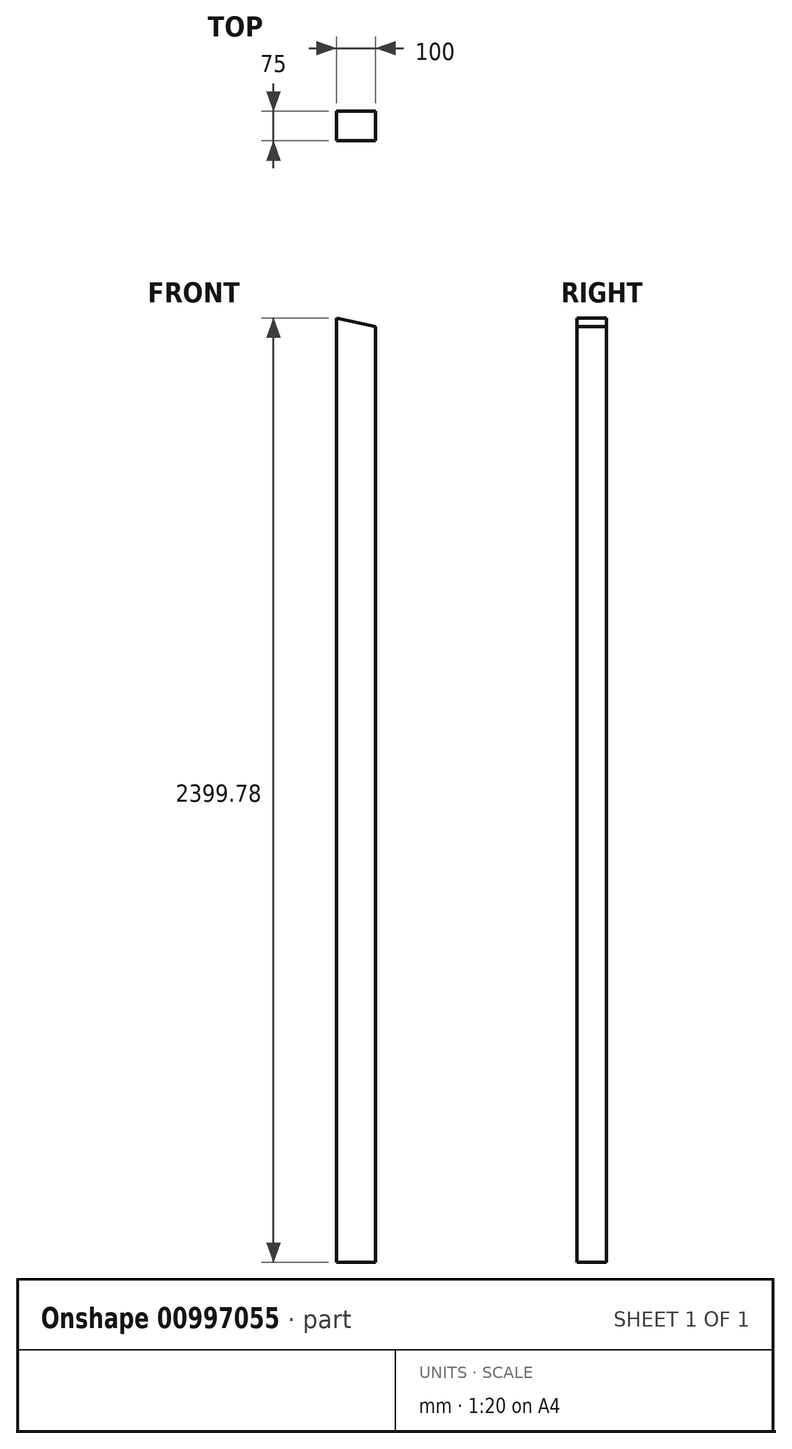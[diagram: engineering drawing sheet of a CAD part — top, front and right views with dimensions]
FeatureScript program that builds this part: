
annotation { "Feature Type Name" : "Feature", "Feature Type Description" : "" }
export const myFeature = defineFeature(function(context is Context, id is Id, definition is map)
    precondition{}
    {
        {
            var Q0;
            Q0=qCreatedBy(makeId("Top.planeOp"),FACE);
            var sketch = newSketch(context, id + "F0", { "sketchPlane" : qUnion([Q0])});
            skLineSegment(sketch, "E0.bottom", {"start": v(-100, 15.8) * mm, "end": v(0, 15.8) * mm});
            skLineSegment(sketch, "E0.top", {"start": v(-100, -59.2) * mm, "end": v(0, -59.2) * mm});
            skLineSegment(sketch, "E0.left", {"start": v(-100, 15.8) * mm, "end": v(-100, -59.2) * mm});
            skLineSegment(sketch, "E0.right", {"start": v(0, 15.8) * mm, "end": v(0, -59.2) * mm});
            skSolve(sketch);
        }
        {
            var Q0;
            Q0=makeQuery(id+"F0.imprint","IMPRINT",FACE,{"disambiguationData":[TD([[makeQuery(id+"F0.imprint","IMPRINT",EDGE,{"derivedFrom":sQuery(id+"F0.wireOp",EDGE,"E0.bottom")}),-1.0]])]});
            extrude(context, id + "F1", {"entities" : qUnion([Q0]), "oppositeDirection" : true, "depth" : 2400 * mm, "offsetDistance" : 25 * mm});
        }
        {
            var Q0;
            Q0=makeQuery(id+"F1.opExtrude","CAP_EDGE",EDGE,{"disambiguationData":[OSD([sQuery(id+"F0.wireOp",EDGE,"E0.right")])],"isStart":true});
            chamfer(context, id + "F2", {"entities" : qUnion([Q0]), "chamferType" : ChamferType.OFFSET_ANGLE, "width" : 101 * mm, "oppositeDirection" : true, "angle" : 12.3 * degree, "tangentPropagation" : true});
        }
    });
